# Revit family: Valve_Trim-Pressure_Balance-Grohe-Eurosmart-14462_Series
name_source: partatom
category: Plumbing Fixtures
units: mm (PartAtom-declared; Revit-internal decimal feet)

## family parameters
Cut with Voids When Loaded = No
Host = Face
OmniClass Number = 23.45.05.14.17
OmniClass Title = Showers
Part Type = Normal
Room Calculation Point = No
Round Connector Dimension = Use Diameter
Shared = Yes

## types (2) — shared parameters
ADA Compliant = Yes
Assembly Code = D2010710
CW Connection = No
CWFU = 3
Default Elevation = 44"
Description = Eurosmart Pressure Balance Trim with Cartridge
HW Connection = No
HWFU = 3
Handle Width (2-3/8" to 3-13/16") = 2 3/8"
Height = 7"
Installation Type = Wall Mounted
Length = 6 1/4"
Manufacturer = Grohe
Price = Prices may vary. Please consult Manufacturer Representative for most up-to-date price list.
Product Documentation Link = https://americanstandard.box.com
Product Page URL = https://www.grohe.us
Revised Date = 05/12/2021
URL = https://www.grohe.us
Vent Connection = No
WFU = 4
Waste Connection = No
Width = 2 3/8"

## per-type parameters (varying)
| type | Finish | Flow Rate | Material |
| 14462000 | Metal-Grohe-000-Starlight Chrome | 5.2 gpm (bottom) and 3.0 gpm (top port) at 45 psi (19L/min.) | Metal-Grohe-000-Starlight Chrome |
| 14462EN0 | Metal-Grohe-EN0-Brushed Nickel Infinity Finish |  | Metal-Grohe-EN0-Brushed Nickel Infinity Finish |

note: column(s) folded — value = type name in every type: Model

## geometry (parser evidence)
native form markers: Sweep x5
no freeform markers — native parametric forms only
